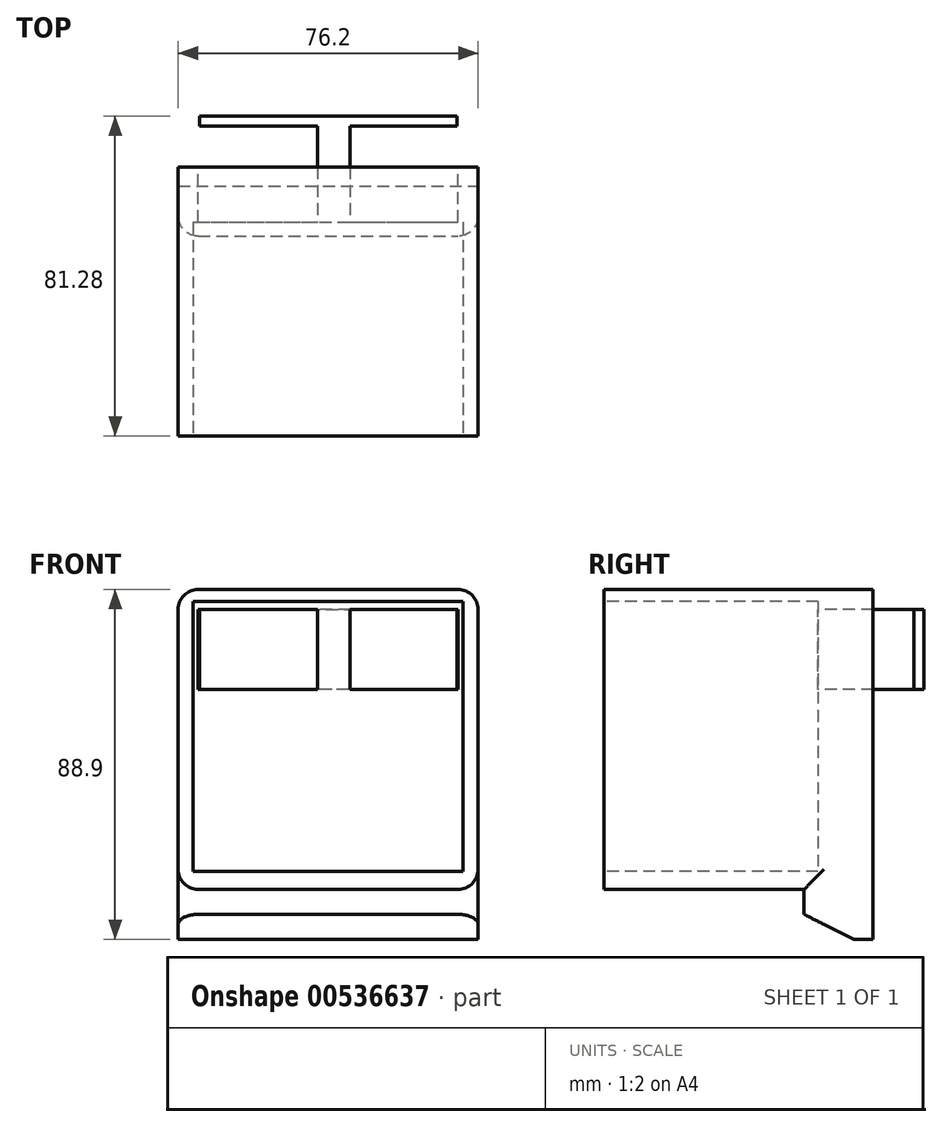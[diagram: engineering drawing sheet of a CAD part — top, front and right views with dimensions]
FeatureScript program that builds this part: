
annotation { "Feature Type Name" : "Feature", "Feature Type Description" : "" }
export const myFeature = defineFeature(function(context is Context, id is Id, definition is map)
    precondition{}
    {
        {
            var Q0;
            Q0=qCreatedBy(makeId("Front.planeOp"),FACE);
            var sketch = newSketch(context, id + "F0", { "sketchPlane" : qUnion([Q0])});
            skLineSegment(sketch, "E0.bottom", {"start": v(-39.53, 34.34) * mm, "end": v(36.67, 34.34) * mm});
            skLineSegment(sketch, "E0.top", {"start": v(-39.53, -41.86) * mm, "end": v(36.67, -41.86) * mm});
            skLineSegment(sketch, "E0.left", {"start": v(-39.53, 34.34) * mm, "end": v(-39.53, -41.86) * mm});
            skLineSegment(sketch, "E0.right", {"start": v(36.67, 34.34) * mm, "end": v(36.67, -41.86) * mm});
            skSolve(sketch);
        }
        {
            var Q0;
            Q0 = qSketchRegion(id + "F0", true);
            extrude(context, id + "F1", {"entities" : qUnion([Q0]), "depth" : 63.5 * mm, "offsetDistance" : 25.4 * mm});
        }
        {
            var Q0;
            Q0=makeQuery(id+"F1.opExtrude","CAP_FACE",FACE,{"disambiguationData":[OSD([sQuery(id+"F0.wireOp",EDGE,"E0.bottom"),sQuery(id+"F0.wireOp",EDGE,"E0.top"),sQuery(id+"F0.wireOp",EDGE,"E0.left"),sQuery(id+"F0.wireOp",EDGE,"E0.right")])],"isStart":false});
            var sketch = newSketch(context, id + "F2", { "sketchPlane" : qUnion([Q0])});
            skLineSegment(sketch, "E1.bottom", {"start": v(-35.8, 31.35) * mm, "end": v(32.78, 31.35) * mm});
            skLineSegment(sketch, "E1.top", {"start": v(-35.8, -37.23) * mm, "end": v(32.78, -37.23) * mm});
            skLineSegment(sketch, "E1.left", {"start": v(-35.8, 31.35) * mm, "end": v(-35.8, -37.23) * mm});
            skLineSegment(sketch, "E1.right", {"start": v(32.78, 31.35) * mm, "end": v(32.78, -37.23) * mm});
            skSolve(sketch);
        }
        {
            var Q0;
            Q0 = qSketchRegion(id + "F2", true);
            extrude(context, id + "F3", {"entities" : qUnion([Q0]), "operationType" : NewBodyOperationType.REMOVE, "oppositeDirection" : true, "depth" : 54.36 * mm, "offsetDistance" : 25.4 * mm});
        }
        {
            var Q0;
            Q0=makeQuery(id+"F1.opExtrude","SWEPT_FACE",FACE,{"disambiguationData":[OSD([sQuery(id+"F0.wireOp",EDGE,"E0.top")])]});
            var sketch = newSketch(context, id + "F4", { "sketchPlane" : qUnion([Q0])});
            skLineSegment(sketch, "E2", {"start": v(-39.53, 0) * mm, "end": v(-39.53, 12.7) * mm});
            skLineSegment(sketch, "E3", {"start": v(-39.53, 12.7) * mm, "end": v(36.67, 12.7) * mm});
            skLineSegment(sketch, "E4", {"start": v(36.67, 12.7) * mm, "end": v(36.67, 0) * mm});
            skLineSegment(sketch, "E5", {"start": v(36.67, 0) * mm, "end": v(-39.53, 0) * mm});
            skSolve(sketch);
        }
        {
            var Q0;
            Q0 = qSketchRegion(id + "F4", true);
            extrude(context, id + "F5", {"entities" : qUnion([Q0]), "operationType" : NewBodyOperationType.ADD, "depth" : 12.7 * mm, "offsetDistance" : 25.4 * mm});
        }
        {
            var Q0;
            Q0=makeQuery(id+"F5.boolean.opBoolean","MERGE",FACE,{"derivedFrom":[makeQuery(id+"F1.opExtrude","SWEPT_FACE",FACE,{"disambiguationData":[OSD([sQuery(id+"F0.wireOp",EDGE,"E0.left")])]}),makeQuery(id+"F5.opExtrude","SWEPT_FACE",FACE,{"disambiguationData":[OSD([sQuery(id+"F4.wireOp",EDGE,"E2")])]})]});
            var sketch = newSketch(context, id + "F6", { "sketchPlane" : qUnion([Q0])});
            skLineSegment(sketch, "E6", {"start": v(0, -54.56) * mm, "end": v(12.7, -48.2) * mm});
            skLineSegment(sketch, "E7", {"start": v(0, -54.56) * mm, "end": v(12.7, -54.56) * mm});
            skLineSegment(sketch, "E8", {"start": v(12.7, -54.56) * mm, "end": v(12.7, -48.2) * mm});
            skSolve(sketch);
        }
        {
            var Q0;
            Q0 = qSketchRegion(id + "F6", true);
            extrude(context, id + "F7", {"entities" : qUnion([Q0]), "operationType" : NewBodyOperationType.REMOVE, "oppositeDirection" : true, "depth" : 81.8 * mm, "offsetDistance" : 25.4 * mm});
        }
        {
            var Q0;
            Q0=makeQuery(id+"F1.opExtrude","SWEPT_EDGE",EDGE,{"disambiguationData":[OSD([sQuery(id+"F0.wireOp",EDGE,"E0.top"),sQuery(id+"F0.wireOp",EDGE,"E0.left")])]});
            var Q1;
            Q1=makeQuery(id+"F1.opExtrude","SWEPT_EDGE",EDGE,{"disambiguationData":[OSD([sQuery(id+"F0.wireOp",EDGE,"E0.top"),sQuery(id+"F0.wireOp",EDGE,"E0.right")])]});
            var Q2;
            Q2=makeQuery(id+"F7.boolean.opBoolean","COPY",EDGE,{"derivedFrom":makeQuery(id+"F7.opExtrude","SWEPT_EDGE",EDGE,{"disambiguationData":[OSD([sQuery(id+"F0.wireOp",EDGE,"E0.top"),sQuery(id+"F0.wireOp",EDGE,"E0.left"),sQuery(id+"F4.wireOp",EDGE,"E2"),sQuery(id+"F4.wireOp",EDGE,"E3"),sQuery(id+"F6.wireOp",EDGE,"E6"),sQuery(id+"F6.wireOp",EDGE,"E8")])]})});
            var Q3;
            Q3=makeQuery(id+"F5.opExtrude","SWEPT_EDGE",EDGE,{"disambiguationData":[OSD([sQuery(id+"F0.wireOp",EDGE,"E0.top"),sQuery(id+"F0.wireOp",EDGE,"E0.left"),sQuery(id+"F4.wireOp",EDGE,"E2"),sQuery(id+"F4.wireOp",EDGE,"E3")])]});
            var Q4;
            Q4=makeQuery(id+"F5.opExtrude","SWEPT_EDGE",EDGE,{"disambiguationData":[OSD([sQuery(id+"F0.wireOp",EDGE,"E0.top"),sQuery(id+"F0.wireOp",EDGE,"E0.right"),sQuery(id+"F4.wireOp",EDGE,"E3"),sQuery(id+"F4.wireOp",EDGE,"E4")])]});
            var Q5;
            Q5=makeQuery(id+"F1.opExtrude","SWEPT_EDGE",EDGE,{"disambiguationData":[OSD([sQuery(id+"F0.wireOp",EDGE,"E0.bottom"),sQuery(id+"F0.wireOp",EDGE,"E0.right")])]});
            var Q6;
            Q6=makeQuery(id+"F1.opExtrude","SWEPT_EDGE",EDGE,{"disambiguationData":[OSD([sQuery(id+"F0.wireOp",EDGE,"E0.bottom"),sQuery(id+"F0.wireOp",EDGE,"E0.left")])]});
            fillet(context, id + "F8", {"entities" : qUnion([Q0, Q1, Q2, Q3, Q4, Q5, Q6]), "radius" : 5.08 * mm, "tangentPropagation" : true, "allowEdgeOverflow" : false});
        }
        {
            var Q0;
            Q0=makeQuery(id+"F5.boolean.opBoolean","MERGE",FACE,{"derivedFrom":[makeQuery(id+"F1.opExtrude","CAP_FACE",FACE,{"disambiguationData":[OSD([sQuery(id+"F0.wireOp",EDGE,"E0.bottom"),sQuery(id+"F0.wireOp",EDGE,"E0.top"),sQuery(id+"F0.wireOp",EDGE,"E0.left"),sQuery(id+"F0.wireOp",EDGE,"E0.right")])],"isStart":true}),makeQuery(id+"F5.opExtrude","SWEPT_FACE",FACE,{"disambiguationData":[OSD([sQuery(id+"F4.wireOp",EDGE,"E5")])]})]});
            var sketch = newSketch(context, id + "F9", { "sketchPlane" : qUnion([Q0])});
            skPoint(sketch, "E9.centerSnap0", {"position": v(1.43, -54.56) * mm});
            skLineSegment(sketch, "E10", {"start": v(-31.6, 8.94) * mm, "end": v(34.45, 8.94) * mm});
            skLineSegment(sketch, "E11", {"start": v(-31.6, 29.26) * mm, "end": v(34.45, 29.26) * mm});
            skLineSegment(sketch, "E12", {"start": v(34.45, 8.94) * mm, "end": v(34.45, 29.26) * mm});
            skLineSegment(sketch, "E13", {"start": v(-31.6, 8.94) * mm, "end": v(-31.6, 29.26) * mm});
            skSolve(sketch);
        }
        {
            var Q0;
            Q0 = qSketchRegion(id + "F9", true);
            extrude(context, id + "F10", {"entities" : qUnion([Q0]), "operationType" : NewBodyOperationType.REMOVE, "oppositeDirection" : true, "depth" : 25.4 * mm, "offsetDistance" : 25.4 * mm});
        }
        {
            var Q0;
            Q0=makeQuery(id+"F10.boolean.opBoolean","COPY",FACE,{"derivedFrom":makeQuery(id+"F10.opExtrude","SWEPT_FACE",FACE,{"disambiguationData":[OSD([sQuery(id+"F9.wireOp",EDGE,"E11")])]})});
            var sketch = newSketch(context, id + "F11", { "sketchPlane" : qUnion([Q0])});
            skLineSegment(sketch, "E14", {"start": v(-4.17, 9.14) * mm, "end": v(-4.17, 0) * mm});
            skLineSegment(sketch, "E15", {"start": v(-4.17, 0) * mm, "end": v(0, 0) * mm});
            skLineSegment(sketch, "E16", {"start": v(0, 0) * mm, "end": v(4.17, 0) * mm});
            skLineSegment(sketch, "E17", {"start": v(4.17, 0) * mm, "end": v(4.17, 9.14) * mm});
            skLineSegment(sketch, "E18", {"start": v(4.17, 9.14) * mm, "end": v(-4.17, 9.14) * mm});
            skSolve(sketch);
        }
        {
            var Q0;
            Q0 = qSketchRegion(id + "F11", true);
            extrude(context, id + "F12", {"entities" : qUnion([Q0]), "operationType" : NewBodyOperationType.ADD, "depth" : 25.4 * mm, "offsetDistance" : 25.4 * mm});
        }
        {
            var Q0;
            Q0=makeQuery(id+"F12.boolean.opBoolean","MERGE",FACE,{"derivedFrom":[makeQuery(id+"F5.boolean.opBoolean","MERGE",FACE,{"derivedFrom":[makeQuery(id+"F1.opExtrude","CAP_FACE",FACE,{"disambiguationData":[OSD([sQuery(id+"F0.wireOp",EDGE,"E0.bottom"),sQuery(id+"F0.wireOp",EDGE,"E0.top"),sQuery(id+"F0.wireOp",EDGE,"E0.left"),sQuery(id+"F0.wireOp",EDGE,"E0.right")])],"isStart":true}),makeQuery(id+"F5.opExtrude","SWEPT_FACE",FACE,{"disambiguationData":[OSD([sQuery(id+"F4.wireOp",EDGE,"E5")])]})]}),makeQuery(id+"F12.opExtrude","SWEPT_FACE",FACE,{"disambiguationData":[OSD([sQuery(id+"F11.wireOp",EDGE,"E15"),sQuery(id+"F11.wireOp",EDGE,"E16")])]})]});
            var sketch = newSketch(context, id + "F13", { "sketchPlane" : qUnion([Q0])});
            skLineSegment(sketch, "E19", {"start": v(4.17, 29.26) * mm, "end": v(-4.17, 29.26) * mm});
            skLineSegment(sketch, "E20", {"start": v(-4.17, 29.26) * mm, "end": v(-4.17, 8.94) * mm});
            skLineSegment(sketch, "E21", {"start": v(-4.17, 8.94) * mm, "end": v(4.17, 8.94) * mm});
            skLineSegment(sketch, "E22", {"start": v(4.17, 8.94) * mm, "end": v(4.17, 29.26) * mm});
            skSolve(sketch);
        }
        {
            var Q0;
            Q0 = qSketchRegion(id + "F13", true);
            extrude(context, id + "F14", {"entities" : qUnion([Q0]), "operationType" : NewBodyOperationType.ADD, "depth" : 17.78 * mm, "offsetDistance" : 25.4 * mm});
        }
        {
            var Q0;
            Q0=makeQuery(id+"F14.boolean.opBoolean","MERGE",FACE,{"derivedFrom":[makeQuery(id+"F12.opExtrude","SWEPT_FACE",FACE,{"disambiguationData":[OSD([sQuery(id+"F11.wireOp",EDGE,"E17")])]}),makeQuery(id+"F14.opExtrude","SWEPT_FACE",FACE,{"disambiguationData":[OSD([sQuery(id+"F13.wireOp",EDGE,"E20")])]})]});
            var sketch = newSketch(context, id + "F15", { "sketchPlane" : qUnion([Q0])});
            skLineSegment(sketch, "E23", {"start": v(17.78, 8.94) * mm, "end": v(15.24, 8.94) * mm});
            skLineSegment(sketch, "E24", {"start": v(15.24, 8.94) * mm, "end": v(15.24, 29.26) * mm});
            skLineSegment(sketch, "E25", {"start": v(15.24, 29.26) * mm, "end": v(17.78, 29.26) * mm});
            skLineSegment(sketch, "E26", {"start": v(17.78, 29.26) * mm, "end": v(17.78, 8.94) * mm});
            skSolve(sketch);
        }
        {
            var Q0;
            Q0 = qSketchRegion(id + "F15", true);
            extrude(context, id + "F16", {"entities" : qUnion([Q0]), "operationType" : NewBodyOperationType.ADD, "depth" : 27.18 * mm, "offsetDistance" : 25.4 * mm});
        }
        {
            var Q0;
            Q0=makeQuery(id+"F14.boolean.opBoolean","MERGE",FACE,{"derivedFrom":[makeQuery(id+"F12.opExtrude","SWEPT_FACE",FACE,{"disambiguationData":[OSD([sQuery(id+"F11.wireOp",EDGE,"E14")])]}),makeQuery(id+"F14.opExtrude","SWEPT_FACE",FACE,{"disambiguationData":[OSD([sQuery(id+"F13.wireOp",EDGE,"E22")])]})]});
            var sketch = newSketch(context, id + "F17", { "sketchPlane" : qUnion([Q0])});
            skLineSegment(sketch, "E27", {"start": v(-17.78, 8.94) * mm, "end": v(-17.78, 29.26) * mm});
            skLineSegment(sketch, "E28", {"start": v(-17.78, 29.26) * mm, "end": v(-15.24, 29.26) * mm});
            skLineSegment(sketch, "E29", {"start": v(-15.24, 29.26) * mm, "end": v(-15.24, 8.94) * mm});
            skPoint(sketch, "E29.endSnap0", {"position": v(-8.9, 8.94) * mm});
            skLineSegment(sketch, "E30", {"start": v(-15.24, 8.94) * mm, "end": v(-17.78, 8.94) * mm});
            skSolve(sketch);
        }
        {
            var Q0;
            Q0 = qSketchRegion(id + "F17", true);
            extrude(context, id + "F18", {"entities" : qUnion([Q0]), "operationType" : NewBodyOperationType.ADD, "depth" : 29.97 * mm, "offsetDistance" : 25.4 * mm});
        }
        {
            var Q0;
            Q0=makeQuery(id+"F12.boolean.opBoolean","MERGE",FACE,{"derivedFrom":[makeQuery(id+"F5.boolean.opBoolean","MERGE",FACE,{"derivedFrom":[makeQuery(id+"F1.opExtrude","CAP_FACE",FACE,{"disambiguationData":[OSD([sQuery(id+"F0.wireOp",EDGE,"E0.bottom"),sQuery(id+"F0.wireOp",EDGE,"E0.top"),sQuery(id+"F0.wireOp",EDGE,"E0.left"),sQuery(id+"F0.wireOp",EDGE,"E0.right")])],"isStart":true}),makeQuery(id+"F5.opExtrude","SWEPT_FACE",FACE,{"disambiguationData":[OSD([sQuery(id+"F4.wireOp",EDGE,"E5")])]})]}),makeQuery(id+"F12.opExtrude","SWEPT_FACE",FACE,{"disambiguationData":[OSD([sQuery(id+"F11.wireOp",EDGE,"E15"),sQuery(id+"F11.wireOp",EDGE,"E16")])]})]});
            var sketch = newSketch(context, id + "F19", { "sketchPlane" : qUnion([Q0])});
            skSolve(sketch);
        }
        {
            var Q0;
            {var subQ8=sQuery(id+"F0.wireOp",EDGE,"E0.bottom");Q0=makeQuery(id+"F19.imprint","IMPRINT",FACE,{"disambiguationData":[TD([[makeQuery(id+"F19.imprint","IMPRINT",EDGE,{"derivedFrom":makeQuery(id+"F1.opExtrude","CAP_EDGE",EDGE,{"disambiguationData":[OSD([subQ8])],"isStart":true})}),1.0]])]});}
            extrude(context, id + "F20", {"entities" : qUnion([Q0]), "operationType" : NewBodyOperationType.ADD, "depth" : 4.83 * mm, "offsetDistance" : 25.4 * mm});
        }
    });
